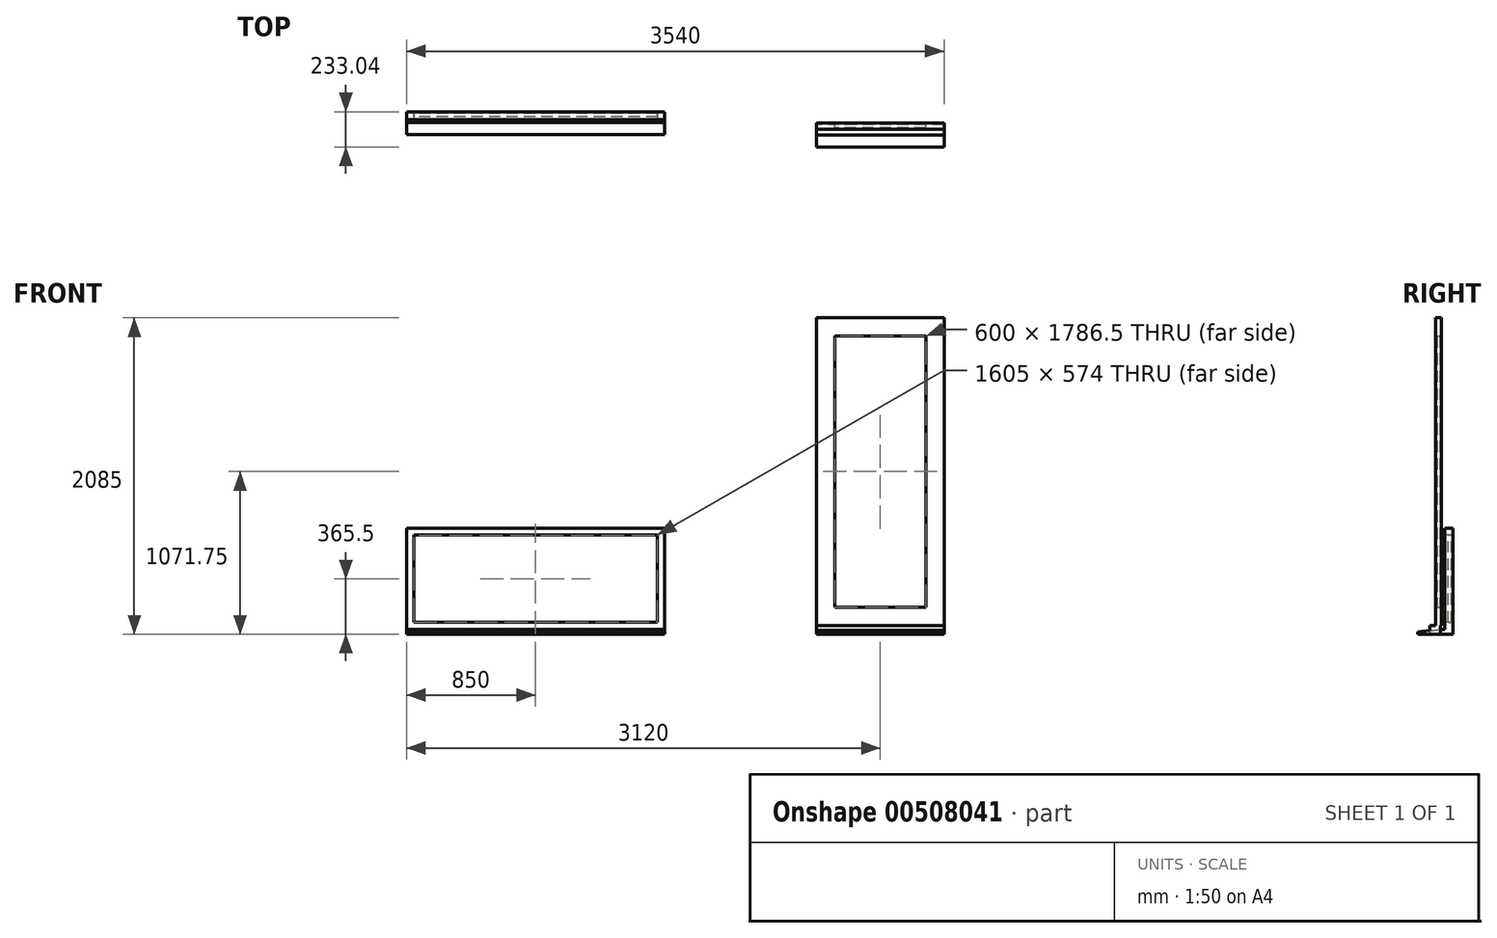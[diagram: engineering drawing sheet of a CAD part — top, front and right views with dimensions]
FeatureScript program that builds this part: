
annotation { "Feature Type Name" : "Feature", "Feature Type Description" : "" }
export const myFeature = defineFeature(function(context is Context, id is Id, definition is map)
    precondition{}
    {
        {
            var Q0;
            Q0=qCreatedBy(makeId("Right.planeOp"),FACE);
            var sketch = newSketch(context, id + "F0", { "sketchPlane" : qUnion([Q0])});
            skLineSegment(sketch, "E0.bottom", {"start": v(83.04, 0) * mm, "end": v(-66.96, 0) * mm});
            skLineSegment(sketch, "E0.top", {"start": v(83.04, 31) * mm, "end": v(-66.96, 31) * mm});
            skLineSegment(sketch, "E0.left", {"start": v(83.04, 0) * mm, "end": v(83.04, 31) * mm});
            skLineSegment(sketch, "E0.right", {"start": v(-66.96, 0) * mm, "end": v(-66.96, 31) * mm});
            skSolve(sketch);
        }
        {
            var Q0;
            Q0=makeQuery(id+"F0.imprint","IMPRINT",FACE,{"disambiguationData":[TD([[makeQuery(id+"F0.imprint","IMPRINT",EDGE,{"derivedFrom":sQuery(id+"F0.wireOp",EDGE,"E0.bottom")}),-1.0]])]});
            extrude(context, id + "F1", {"entities" : qUnion([Q0]), "oppositeDirection" : true, "depth" : 1700 * mm});
        }
        {
            var Q0;
            Q0=makeQuery(id+"F1.opExtrude","SWEPT_FACE",FACE,{"disambiguationData":[OSD([sQuery(id+"F0.wireOp",EDGE,"E0.left")])]});
            var sketch = newSketch(context, id + "F2", { "sketchPlane" : qUnion([Q0])});
            skLineSegment(sketch, "E1.bottom", {"start": v(0, 31) * mm, "end": v(1700, 31) * mm});
            skLineSegment(sketch, "E1.top", {"start": v(0, 700) * mm, "end": v(1700, 700) * mm});
            skLineSegment(sketch, "E1.left", {"start": v(0, 31) * mm, "end": v(0, 700) * mm});
            skLineSegment(sketch, "E1.right", {"start": v(1700, 31) * mm, "end": v(1700, 700) * mm});
            skSolve(sketch);
        }
        {
            var Q0;
            Q0=qCreatedBy(makeId("Right.planeOp"),FACE);
            var sketch = newSketch(context, id + "F3", { "sketchPlane" : qUnion([Q0])});
            skLineSegment(sketch, "E2.bottom", {"start": v(83.04, 31) * mm, "end": v(30.04, 31) * mm});
            skLineSegment(sketch, "E2.top", {"start": v(83.04, 78.5) * mm, "end": v(30.04, 78.5) * mm});
            skLineSegment(sketch, "E2.left", {"start": v(83.04, 31) * mm, "end": v(83.04, 78.5) * mm});
            skLineSegment(sketch, "E2.right", {"start": v(30.04, 31) * mm, "end": v(30.04, 78.5) * mm});
            skSolve(sketch);
        }
        {
            var Q0;
            Q0=makeQuery(id+"F3.imprint","IMPRINT",FACE,{"disambiguationData":[TD([[makeQuery(id+"F3.imprint","IMPRINT",EDGE,{"derivedFrom":sQuery(id+"F3.wireOp",EDGE,"E2.bottom")}),-1.0]])]});
            var Q1;
            Q1 = qConstructionFilter(qBodyType(qCreatedBy(id + "F2" ,EDGE), BodyType.WIRE), ConstructionObject.NO);
            sweep(context, id + "F4", {"operationType" : NewBodyOperationType.ADD, "profiles" : qUnion([Q0]), "path" : qUnion([Q1])});
        }
        {
            var Q0;
            Q0=makeQuery(id+"F4.boolean.opBoolean","MERGE",FACE,{"derivedFrom":[makeQuery(id+"F1.opExtrude","SWEPT_FACE",FACE,{"disambiguationData":[OSD([sQuery(id+"F0.wireOp",EDGE,"E0.left")])]}),makeQuery(id+"F4.opSweep","SWEPT_FACE",FACE,{"disambiguationData":[OSD([sQuery(id+"F2.wireOp",EDGE,"E1.bottom"),sQuery(id+"F3.wireOp",EDGE,"E2.left")])]})]});
            cPlane(context, id + "F5", {"entities" : qUnion([Q0]), "cplaneType" : CPlaneType.OFFSET, "offset" : 10 * mm, "oppositeDirection" : true, "width" : 150 * mm, "height" : 150 * mm});
        }
        {
            var Q0;
            Q0=qCreatedBy(id+"F5.planeOp",FACE);
            var sketch = newSketch(context, id + "F6", { "sketchPlane" : qUnion([Q0])});
            skLineSegment(sketch, "E3.bottom", {"start": v(47.5, 78.5) * mm, "end": v(1652.5, 78.5) * mm});
            skLineSegment(sketch, "E3.top", {"start": v(47.5, 652.5) * mm, "end": v(1652.5, 652.5) * mm});
            skLineSegment(sketch, "E3.left", {"start": v(47.5, 78.5) * mm, "end": v(47.5, 652.5) * mm});
            skLineSegment(sketch, "E3.right", {"start": v(1652.5, 78.5) * mm, "end": v(1652.5, 652.5) * mm});
            skSolve(sketch);
        }
        {
            var Q0;
            Q0=makeQuery(id+"F6.imprint","IMPRINT",FACE,{"disambiguationData":[TD([[makeQuery(id+"F6.imprint","IMPRINT",EDGE,{"derivedFrom":sQuery(id+"F6.wireOp",EDGE,"E3.bottom")}),1.0]])]});
            extrude(context, id + "F7", {"entities" : qUnion([Q0]), "oppositeDirection" : true, "depth" : 22 * mm});
        }
        {
            var Q0;
            Q0=qCreatedBy(makeId("Right.planeOp"),FACE);
            cPlane(context, id + "F8", {"entities" : qUnion([Q0]), "cplaneType" : CPlaneType.OFFSET, "offset" : 1000 * mm, "width" : 150 * mm, "height" : 150 * mm});
        }
        {
            var Q0;
            Q0=qCreatedBy(id+"F8.planeOp",FACE);
            var sketch = newSketch(context, id + "F9", { "sketchPlane" : qUnion([Q0])});
            skLineSegment(sketch, "E4.bottom", {"start": v(0, 0) * mm, "end": v(-150, 0) * mm});
            skLineSegment(sketch, "E4.top", {"start": v(-70, 25) * mm, "end": v(-150, 25) * mm});
            skLineSegment(sketch, "E4.left", {"start": v(0, 0) * mm, "end": v(0, 25) * mm});
            skLineSegment(sketch, "E4.right", {"start": v(-150, 0) * mm, "end": v(-150, 25) * mm});
            skLineSegment(sketch, "E5.top", {"start": v(0, 58.5) * mm, "end": v(-70, 58.5) * mm});
            skLineSegment(sketch, "E5.left", {"start": v(0, 25) * mm, "end": v(0, 58.5) * mm});
            skLineSegment(sketch, "E5.right", {"start": v(-70, 25) * mm, "end": v(-70, 58.5) * mm});
            skSolve(sketch);
        }
        {
            var Q0;
            Q0=makeQuery(id+"F9.imprint","IMPRINT",FACE,{"disambiguationData":[TD([[makeQuery(id+"F9.imprint","IMPRINT",EDGE,{"derivedFrom":sQuery(id+"F9.wireOp",EDGE,"E4.bottom")}),-1.0]])]});
            extrude(context, id + "F10", {"entities" : qUnion([Q0]), "depth" : 840 * mm});
        }
        {
            var Q0;
            Q0=makeQuery(id+"F10.opExtrude","SWEPT_FACE",FACE,{"disambiguationData":[OSD([sQuery(id+"F9.wireOp",EDGE,"E4.left"),sQuery(id+"F9.wireOp",EDGE,"E5.left")])]});
            cPlane(context, id + "F11", {"entities" : qUnion([Q0]), "cplaneType" : CPlaneType.OFFSET, "offset" : 8 * mm, "width" : 150 * mm, "height" : 150 * mm});
        }
        {
            var Q0;
            Q0=qCreatedBy(id+"F11.planeOp",FACE);
            var sketch = newSketch(context, id + "F12", { "sketchPlane" : qUnion([Q0])});
            skLineSegment(sketch, "E6.bottom", {"start": v(-1000, 58.5) * mm, "end": v(-1840, 58.5) * mm});
            skLineSegment(sketch, "E6.top", {"start": v(-1000, 2085) * mm, "end": v(-1840, 2085) * mm});
            skLineSegment(sketch, "E6.left", {"start": v(-1000, 58.5) * mm, "end": v(-1000, 2085) * mm});
            skLineSegment(sketch, "E6.right", {"start": v(-1840, 58.5) * mm, "end": v(-1840, 2085) * mm});
            skLineSegment(sketch, "E7.bottom", {"start": v(-1720, 1965) * mm, "end": v(-1120, 1965) * mm});
            skLineSegment(sketch, "E7.top", {"start": v(-1720, 178.5) * mm, "end": v(-1120, 178.5) * mm});
            skLineSegment(sketch, "E7.left", {"start": v(-1720, 1965) * mm, "end": v(-1720, 178.5) * mm});
            skLineSegment(sketch, "E7.right", {"start": v(-1120, 1965) * mm, "end": v(-1120, 178.5) * mm});
            skSolve(sketch);
        }
        {
            var Q0;
            Q0=makeQuery(id+"F12.imprint","IMPRINT",FACE,{"disambiguationData":[TD([[makeQuery(id+"F12.imprint","IMPRINT",EDGE,{"derivedFrom":sQuery(id+"F12.wireOp",EDGE,"E6.bottom")}),-1.0]])]});
            extrude(context, id + "F13", {"entities" : qUnion([Q0]), "operationType" : NewBodyOperationType.ADD, "oppositeDirection" : true, "depth" : 40 * mm});
        }
        {
            var Q0;
            Q0=makeQuery(id+"F13.opExtrude","CAP_FACE",FACE,{"disambiguationData":[OSD([sQuery(id+"F12.wireOp",EDGE,"E6.bottom"),sQuery(id+"F12.wireOp",EDGE,"E6.top"),sQuery(id+"F12.wireOp",EDGE,"E6.left"),sQuery(id+"F12.wireOp",EDGE,"E6.right"),sQuery(id+"F12.wireOp",EDGE,"E7.bottom"),sQuery(id+"F12.wireOp",EDGE,"E7.top"),sQuery(id+"F12.wireOp",EDGE,"E7.left"),sQuery(id+"F12.wireOp",EDGE,"E7.right")])],"isStart":true});
            cPlane(context, id + "F14", {"entities" : qUnion([Q0]), "cplaneType" : CPlaneType.OFFSET, "offset" : 10 * mm, "oppositeDirection" : true, "width" : 150 * mm, "height" : 150 * mm});
        }
        {
            var Q0;
            Q0=qCreatedBy(id+"F14.planeOp",FACE);
            var sketch = newSketch(context, id + "F15", { "sketchPlane" : qUnion([Q0])});
            skLineSegment(sketch, "E8.bottom", {"start": v(-1720, 1965) * mm, "end": v(-1120, 1965) * mm});
            skLineSegment(sketch, "E8.top", {"start": v(-1720, 178.5) * mm, "end": v(-1120, 178.5) * mm});
            skLineSegment(sketch, "E8.left", {"start": v(-1720, 1965) * mm, "end": v(-1720, 178.5) * mm});
            skLineSegment(sketch, "E8.right", {"start": v(-1120, 1965) * mm, "end": v(-1120, 178.5) * mm});
            skSolve(sketch);
        }
        {
            var Q0;
            Q0 = qSketchRegion(id + "F15", true);
            extrude(context, id + "F16", {"entities" : qUnion([Q0]), "oppositeDirection" : true, "depth" : 20 * mm});
        }
        {
            var Q0;
            Q0=makeQuery(id+"F1.opExtrude","SWEPT_EDGE",EDGE,{"disambiguationData":[OSD([sQuery(id+"F0.wireOp",EDGE,"E0.top"),sQuery(id+"F0.wireOp",EDGE,"E0.right")])]});
            chamfer(context, id + "F17", {"entities" : qUnion([Q0]), "chamferType" : ChamferType.TWO_OFFSETS, "width1" : 80 * mm, "oppositeDirection" : false, "width2" : 8 * mm, "tangentPropagation" : true});
        }
        {
            var Q0;
            Q0=makeQuery(id+"F10.opExtrude","SWEPT_EDGE",EDGE,{"disambiguationData":[OSD([sQuery(id+"F9.wireOp",EDGE,"E4.top"),sQuery(id+"F9.wireOp",EDGE,"E4.right")])]});
            chamfer(context, id + "F18", {"entities" : qUnion([Q0]), "chamferType" : ChamferType.TWO_OFFSETS, "width1" : 8 * mm, "oppositeDirection" : false, "width2" : 80 * mm, "tangentPropagation" : true});
        }
    });
